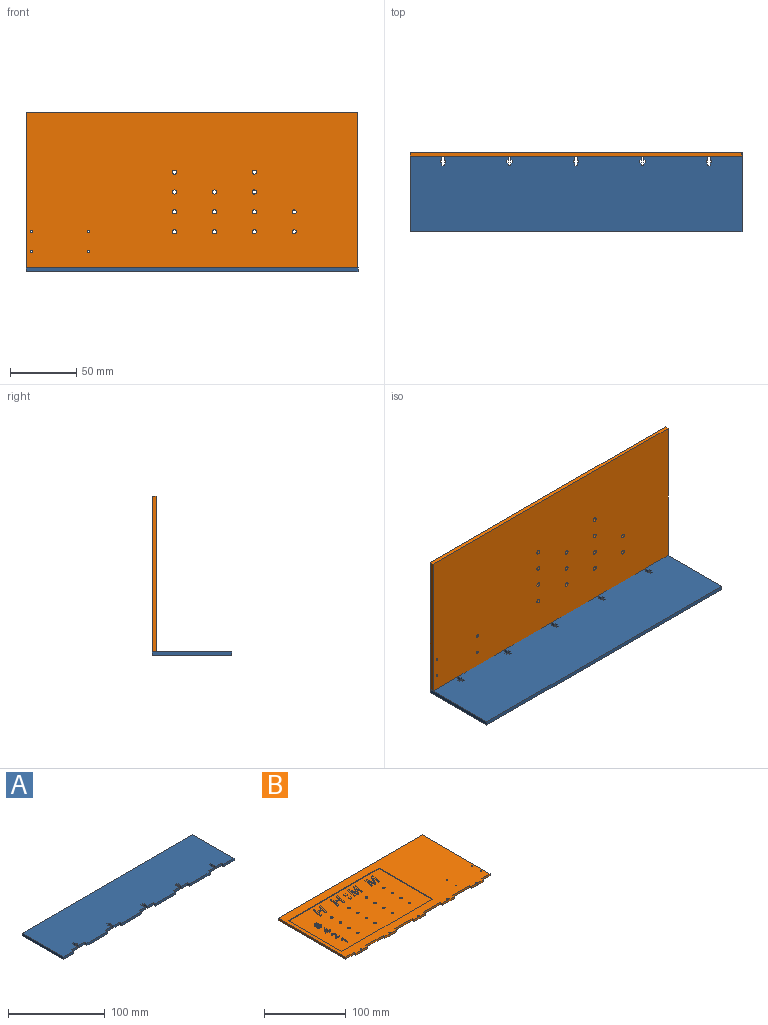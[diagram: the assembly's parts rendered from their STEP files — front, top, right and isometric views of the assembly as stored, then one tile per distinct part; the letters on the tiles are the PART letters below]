
ASSEMBLY  parts=2 mates=1
PART A: 86 faces, bbox 250x60x3 mm
  f0: plane 3x3mm, normal (-1,0,0), area 9mm2, adj f1,f83,f84,f85
  f1: plane 30x3mm, normal (0,-1,0), area 90mm2, adj f0,f2,f84,f85
  f2: plane 3x3mm, normal (1,0,0), area 9mm2, adj f1,f3,f84,f85
  f3: plane 9x3mm, normal (0,-1,0), area 27mm2, adj f2,f4,f84,f85
  f4: plane 3.04x3mm, normal (1,0,0), area 9.1mm2, adj f3,f5,f84,f85
  f5: plane 3x1mm, normal (0,1,0), area 3mm2, adj f4,f6,f84,f85
  f6: plane 3x2mm, normal (1,0,0), area 6mm2, adj f5,f7,f84,f85
  f7: plane 3x1mm, normal (0,-1,0), area 3mm2, adj f6,f8,f84,f85
  f8: plane 3x1.96mm, normal (1,0,0), area 5.9mm2, adj f7,f9,f84,f85
  f9: plane 3x2mm, normal (0,-1,0), area 6mm2, adj f8,f10,f84,f85
  f10: plane 3x1.96mm, normal (-1,0,0), area 5.9mm2, adj f9,f11,f84,f85
  f11: plane 3x1mm, normal (0,-1,0), area 3mm2, adj f10,f12,f84,f85
  f12: plane 3x2mm, normal (-1,0,0), area 6mm2, adj f11,f13,f84,f85
  f13: plane 3x1mm, normal (0,1,0), area 3mm2, adj f12,f14,f84,f85
  f14: plane 3.04x3mm, normal (-1,0,0), area 9.1mm2, adj f13,f15,f84,f85
  f15: plane 9x3mm, normal (0,-1,0), area 27mm2, adj f14,f16,f84,f85
  f16: plane 3x3mm, normal (-1,0,0), area 9mm2, adj f15,f17,f84,f85
  f17: plane 15x3mm, normal (0,-1,0), area 45mm2, adj f16,f18,f84,f85
  f18: plane 60x3mm, normal (1,0,0), area 180mm2, adj f17,f19,f84,f85
  f19: plane 250x3mm, normal (0,1,0), area 750mm2, adj f18,f20,f84,f85
  f20: plane 60x3mm, normal (-1,0,0), area 180mm2, adj f19,f21,f84,f85
  f21: plane 15x3mm, normal (0,-1,0), area 45mm2, adj f20,f22,f84,f85
  f22: plane 3x3mm, normal (1,0,0), area 9mm2, adj f21,f23,f84,f85
  f23: plane 9x3mm, normal (0,-1,0), area 27mm2, adj f22,f24,f84,f85
  f24: plane 3.04x3mm, normal (1,0,0), area 9.1mm2, adj f23,f25,f84,f85
  f25: plane 3x1mm, normal (0,1,0), area 3mm2, adj f24,f26,f84,f85
  f26: plane 3x2mm, normal (1,0,0), area 6mm2, adj f25,f27,f84,f85
  f27: plane 3x1mm, normal (0,-1,0), area 3mm2, adj f26,f28,f84,f85
  f28: plane 3x1.96mm, normal (1,0,0), area 5.9mm2, adj f27,f29,f84,f85
  f29: plane 3x2mm, normal (0,-1,0), area 6mm2, adj f28,f30,f84,f85
  f30: plane 3x1.96mm, normal (-1,0,0), area 5.9mm2, adj f29,f31,f84,f85
  f31: plane 3x1mm, normal (0,-1,0), area 3mm2, adj f30,f32,f84,f85
  f32: plane 3x2mm, normal (-1,0,0), area 6mm2, adj f31,f33,f84,f85
  f33: plane 3x1mm, normal (0,1,0), area 3mm2, adj f32,f34,f84,f85
  f34: plane 3.04x3mm, normal (-1,0,0), area 9.1mm2, adj f33,f35,f84,f85
  f35: plane 9x3mm, normal (0,-1,0), area 27mm2, adj f34,f36,f84,f85
  f36: plane 3x3mm, normal (-1,0,0), area 9mm2, adj f35,f37,f84,f85
  f37: plane 30x3mm, normal (0,-1,0), area 90mm2, adj f36,f38,f84,f85
  f38: plane 3x3mm, normal (1,0,0), area 9mm2, adj f37,f39,f84,f85
  f39: plane 9x3mm, normal (0,-1,0), area 27mm2, adj f38,f40,f84,f85
  f40: plane 3.04x3mm, normal (1,0,0), area 9.1mm2, adj f39,f41,f84,f85
  f41: plane 3x1mm, normal (0,1,0), area 3mm2, adj f40,f42,f84,f85
  f42: plane 3x2mm, normal (1,0,0), area 6mm2, adj f41,f43,f84,f85
  f43: plane 3x1mm, normal (0,-1,0), area 3mm2, adj f42,f44,f84,f85
  f44: plane 3x1.96mm, normal (1,0,0), area 5.9mm2, adj f43,f45,f84,f85
  f45: plane 3x2mm, normal (0,-1,0), area 6mm2, adj f44,f46,f84,f85
  f46: plane 3x1.96mm, normal (-1,0,0), area 5.9mm2, adj f45,f47,f84,f85
  f47: plane 3x1mm, normal (0,-1,0), area 3mm2, adj f46,f48,f84,f85
  f48: plane 3x2mm, normal (-1,0,0), area 6mm2, adj f47,f49,f84,f85
  f49: plane 3x1mm, normal (0,1,0), area 3mm2, adj f48,f50,f84,f85
  f50: plane 3.04x3mm, normal (-1,0,0), area 9.1mm2, adj f49,f51,f84,f85
  f51: plane 9x3mm, normal (0,-1,0), area 27mm2, adj f50,f52,f84,f85
  f52: plane 3x3mm, normal (-1,0,0), area 9mm2, adj f51,f53,f84,f85
  f53: plane 30x3mm, normal (0,-1,0), area 90mm2, adj f52,f54,f84,f85
  f54: plane 3x3mm, normal (1,0,0), area 9mm2, adj f53,f55,f84,f85
  f55: plane 9x3mm, normal (0,-1,0), area 27mm2, adj f54,f56,f84,f85
  f56: plane 3.04x3mm, normal (1,0,0), area 9.1mm2, adj f55,f57,f84,f85
  f57: plane 3x1mm, normal (0,1,0), area 3mm2, adj f56,f58,f84,f85
  f58: plane 3x2mm, normal (1,0,0), area 6mm2, adj f57,f59,f84,f85
  f59: plane 3x1mm, normal (0,-1,0), area 3mm2, adj f58,f60,f84,f85
  f60: plane 3x1.96mm, normal (1,0,0), area 5.9mm2, adj f59,f61,f84,f85
  f61: plane 3x2mm, normal (0,-1,0), area 6mm2, adj f60,f62,f84,f85
  f62: plane 3x1.96mm, normal (-1,0,0), area 5.9mm2, adj f61,f63,f84,f85
  f63: plane 3x1mm, normal (0,-1,0), area 3mm2, adj f62,f64,f84,f85
  f64: plane 3x2mm, normal (-1,0,0), area 6mm2, adj f63,f65,f84,f85
  f65: plane 3x1mm, normal (0,1,0), area 3mm2, adj f64,f66,f84,f85
  f66: plane 3.04x3mm, normal (-1,0,0), area 9.1mm2, adj f65,f67,f84,f85
  f67: plane 9x3mm, normal (0,-1,0), area 27mm2, adj f66,f68,f84,f85
  f68: plane 3x3mm, normal (-1,0,0), area 9mm2, adj f67,f69,f84,f85
  f69: plane 30x3mm, normal (0,-1,0), area 90mm2, adj f68,f70,f84,f85
  f70: plane 3x3mm, normal (1,0,0), area 9mm2, adj f69,f71,f84,f85
  f71: plane 9x3mm, normal (0,-1,0), area 27mm2, adj f70,f72,f84,f85
  f72: plane 3.04x3mm, normal (1,0,0), area 9.1mm2, adj f71,f73,f84,f85
  f73: plane 3x1mm, normal (0,1,0), area 3mm2, adj f72,f74,f84,f85
  f74: plane 3x2mm, normal (1,0,0), area 6mm2, adj f73,f75,f84,f85
  f75: plane 3x1mm, normal (0,-1,0), area 3mm2, adj f74,f76,f84,f85
  f76: plane 3x1.96mm, normal (1,0,0), area 5.9mm2, adj f75,f77,f84,f85
  f77: plane 3x2mm, normal (0,-1,0), area 6mm2, adj f76,f78,f84,f85
  f78: plane 3x1.96mm, normal (-1,0,0), area 5.9mm2, adj f77,f79,f84,f85
  f79: plane 3x1mm, normal (0,-1,0), area 3mm2, adj f78,f80,f84,f85
  f80: plane 3x2mm, normal (-1,0,0), area 6mm2, adj f79,f81,f84,f85
  f81: plane 3x1mm, normal (0,1,0), area 3mm2, adj f80,f82,f84,f85
  f82: plane 3.04x3mm, normal (-1,0,0), area 9.1mm2, adj f81,f83,f84,f85
  f83: plane 9x3mm, normal (0,-1,0), area 27mm2, adj f0,f82,f84,f85
  f84: plane 250x60mm, normal (0,0,1), area 14610mm2, adj f0,f1,f2,f3,f4,f5,f6,f7
  f85: plane 250x60mm, normal (0,0,-1), area 14610mm2, adj f0,f1,f2,f3,f4,f5,f6,f7
PART B: 219 faces, bbox 250x120x3 mm
  f0: cylinder r=1.55mm len=3.1mm, axis (0,0,1), area 19.5mm2, adj f46,f180
  f1: cylinder r=1.55mm len=3.1mm, axis (0,0,1), area 19.5mm2, adj f46,f180
  f2: cylinder r=1.55mm len=3.1mm, axis (0,0,1), area 19.5mm2, adj f46,f180
  f3: cylinder r=1.55mm len=3.1mm, axis (0,0,1), area 19.5mm2, adj f46,f180
  f4: cylinder r=1.55mm len=3.1mm, axis (0,0,1), area 19.5mm2, adj f46,f180
  f5: cylinder r=1.55mm len=3.1mm, axis (0,0,1), area 19.5mm2, adj f46,f180
  f6: cylinder r=1.55mm len=3.1mm, axis (0,0,1), area 19.5mm2, adj f46,f180
  f7: cylinder r=1.55mm len=3.1mm, axis (0,0,1), area 19.5mm2, adj f46,f180
  f8: cylinder r=1.55mm len=3.1mm, axis (0,0,1), area 19.5mm2, adj f46,f180
  f9: cylinder r=1.55mm len=3.1mm, axis (0,0,1), area 19.5mm2, adj f46,f180
  f10: cylinder r=1.55mm len=3.1mm, axis (0,0,1), area 19.5mm2, adj f46,f180
  f11: cylinder r=1.55mm len=3.1mm, axis (0,0,1), area 19.5mm2, adj f46,f180
  f12: cylinder r=1.55mm len=3.1mm, axis (0,0,1), area 19.5mm2, adj f46,f180
  f13: plane 30x3mm, normal (0,-1,0), area 90mm2, adj f14,f41,f46,f47
  f14: plane 3x3mm, normal (-1,0,0), area 9mm2, adj f13,f15,f46,f47
  f15: plane 20x3mm, normal (0,-1,0), area 60mm2, adj f14,f16,f46,f47
  f16: plane 3x3mm, normal (1,0,0), area 9mm2, adj f15,f17,f46,f47
  f17: plane 30x3mm, normal (0,-1,0), area 90mm2, adj f16,f18,f46,f47
  f18: plane 3x3mm, normal (-1,0,0), area 9mm2, adj f17,f19,f46,f47
  f19: plane 20x3mm, normal (0,-1,0), area 60mm2, adj f18,f20,f46,f47
  f20: plane 3x3mm, normal (1,0,0), area 9mm2, adj f19,f21,f46,f47
  f21: plane 30x3mm, normal (0,-1,0), area 90mm2, adj f20,f22,f46,f47
  f22: plane 3x3mm, normal (-1,0,0), area 9mm2, adj f21,f23,f46,f47
  f23: plane 20x3mm, normal (0,-1,0), area 60mm2, adj f22,f24,f46,f47
  f24: plane 3x3mm, normal (1,0,0), area 9mm2, adj f23,f25,f46,f47
  f25: plane 30x3mm, normal (0,-1,0), area 90mm2, adj f24,f26,f46,f47
  f26: plane 3x3mm, normal (-1,0,0), area 9mm2, adj f25,f27,f46,f47
  f27: plane 20x3mm, normal (0,-1,0), area 60mm2, adj f26,f28,f46,f47
  f28: plane 3x3mm, normal (1,0,0), area 9mm2, adj f27,f29,f46,f47
  f29: plane 15x3mm, normal (0,-1,0), area 45mm2, adj f28,f30,f46,f47
  f30: plane 117x3mm, normal (1,0,0), area 351mm2, adj f29,f31,f46,f47
  f31: plane 250x3mm, normal (0,1,0), area 750mm2, adj f30,f32,f46,f47
  f32: plane 117x3mm, normal (-1,0,0), area 351mm2, adj f31,f33,f46,f47
  f33: plane 15x3mm, normal (0,-1,0), area 45mm2, adj f32,f34,f46,f47
  f34: plane 3x3mm, normal (-1,0,0), area 9mm2, adj f33,f35,f46,f47
  f35: plane 20x3mm, normal (0,-1,0), area 60mm2, adj f34,f41,f46,f47
  f36: cylinder r=1.05mm len=3mm, axis (0,0,1), area 19.8mm2, adj f46,f47
  f37: cylinder r=1.05mm len=3mm, axis (0,0,1), area 19.8mm2, adj f46,f47
  f38: cylinder r=1.05mm len=3mm, axis (0,0,1), area 19.8mm2, adj f46,f47
  f39: cylinder r=1.05mm len=3mm, axis (0,0,1), area 19.8mm2, adj f46,f47
  f40: cylinder r=1.05mm len=3mm, axis (0,0,1), area 19.8mm2, adj f46,f47
  f41: plane 3x3mm, normal (1,0,0), area 9mm2, adj f13,f35,f46,f47
  f42: cylinder r=0.89mm len=3mm, axis (0,0,1), area 16.8mm2, adj f46,f47
  f43: cylinder r=0.89mm len=3mm, axis (0,0,1), area 16.8mm2, adj f46,f47
  f44: cylinder r=0.89mm len=3mm, axis (0,0,1), area 16.8mm2, adj f46,f47
  f45: cylinder r=0.89mm len=3mm, axis (0,0,1), area 16.8mm2, adj f46,f47
  f46: plane 250x120mm, normal (0,0,-1), area 29424.6mm2, adj f0,f1,f2,f3,f4,f5,f6,f7
  f47: plane 250x120mm, normal (0,0,1), area 14951.8mm2, adj f13,f14,f15,f16,f17,f18,f19,f20
  f48: plane 92.55x1mm, normal (1,0,0), area 92.5mm2, adj f47,f49,f179,f180
  f49: plane 157.45x1mm, normal (0,1,0), area 157.4mm2, adj f47,f48,f50,f180
  f50: plane 92.55x1mm, normal (-1,0,0), area 92.5mm2, adj f47,f49,f179,f180
  f51: plane 6.67x1mm, normal (1,0,0), area 6.7mm2, adj f52,f166,f180,f193
  f52: plane 1.47x1mm, normal (0,1,0), area 1.5mm2, adj f51,f53,f180,f193
  f53: plane 1.02x1mm, normal (1,0,0), area 1mm2, adj f52,f54,f180,f193
  f54: plane 1.47x1mm, normal (0,-1,0), area 1.5mm2, adj f53,f55,f180,f193
  f55: plane 2.28x1mm, normal (1,0,0), area 2.3mm2, adj f54,f56,f180,f193
  f56: plane 1.08x1mm, normal (0,-1,0), area 1.1mm2, adj f55,f57,f180,f193
  f57: plane 2.28x1mm, normal (-1,0,0), area 2.3mm2, adj f56,f58,f180,f193
  f58: plane 4.82x1mm, normal (0,-1,0), area 4.8mm2, adj f57,f59,f180,f193
  f59: plane 1x0.98mm, normal (-1,0,0), area 1mm2, adj f58,f60,f180,f193
  f60: plane 6.71x4.71mm, normal (-0.82,0.57,0), area 8.2mm2, adj f59,f166,f180,f193
  f61: plane 7.8x1mm, normal (0,-1,0), area 7.8mm2, adj f62,f167,f180,f192
  f62: plane 6.64x1.29mm, normal (0.98,-0.19,0), area 6.8mm2, adj f61,f63,f180,f192
  f63: plane 1.94x1mm, normal (0,-1,0), area 1.9mm2, adj f62,f64,f180,f192
  f64: plane 14.33x2.79mm, normal (-0.98,0.19,0), area 14.6mm2, adj f63,f65,f180,f192
  f65: plane 1.94x1mm, normal (0,1,0), area 1.9mm2, adj f64,f66,f180,f192
  f66: plane 6.06x1.18mm, normal (0.98,-0.19,0), area 6.2mm2, adj f65,f67,f180,f192
  f67: plane 7.8x1mm, normal (0,1,0), area 7.8mm2, adj f66,f68,f180,f192
  f68: plane 6.06x1.18mm, normal (-0.98,0.19,0), area 6.2mm2, adj f67,f69,f180,f192
  f69: plane 1.89x1mm, normal (0,1,0), area 1.9mm2, adj f68,f70,f180,f192
  f70: plane 14.33x2.79mm, normal (0.98,-0.19,0), area 14.6mm2, adj f69,f71,f180,f192
  f71: plane 1.89x1mm, normal (0,-1,0), area 1.9mm2, adj f70,f167,f180,f192
  f72: plane 1.89x1mm, normal (0,1,0), area 1.9mm2, adj f73,f168,f180,f191
  f73: plane 14.33x2.79mm, normal (0.98,-0.19,0), area 14.6mm2, adj f72,f74,f180,f191
  f74: plane 1.89x1mm, normal (0,-1,0), area 1.9mm2, adj f73,f75,f180,f191
  f75: plane 6.64x1.29mm, normal (-0.98,0.19,0), area 6.8mm2, adj f74,f76,f180,f191
  f76: plane 7.8x1mm, normal (0,-1,0), area 7.8mm2, adj f75,f77,f180,f191
  f77: plane 6.64x1.29mm, normal (0.98,-0.19,0), area 6.8mm2, adj f76,f78,f180,f191
  f78: plane 1.94x1mm, normal (0,-1,0), area 1.9mm2, adj f77,f79,f180,f191
  f79: plane 14.33x2.79mm, normal (-0.98,0.19,0), area 14.6mm2, adj f78,f80,f180,f191
  f80: plane 1.94x1mm, normal (0,1,0), area 1.9mm2, adj f79,f81,f180,f191
  f81: plane 6.06x1.18mm, normal (0.98,-0.19,0), area 6.2mm2, adj f80,f82,f180,f191
  f82: plane 7.8x1mm, normal (0,1,0), area 7.8mm2, adj f81,f168,f180,f191
  f83: plane 3.06x1mm, normal (1,0,0), area 3.1mm2, adj f84,f169,f180,f190
  f84: plane 3.13x1mm, normal (0,-1,0), area 3.1mm2, adj f83,f85,f180,f190
  f85: plane 3.06x1mm, normal (-1,0,0), area 3.1mm2, adj f84,f169,f180,f190
  f86: plane 3.05x1mm, normal (1,0,0), area 3.1mm2, adj f87,f170,f180,f189
  f87: plane 3.13x1mm, normal (0,-1,0), area 3.1mm2, adj f86,f88,f180,f189
  f88: plane 3.05x1mm, normal (-1,0,0), area 3.1mm2, adj f87,f170,f180,f189
  f89: plane 9.86x5.63mm, normal (-0.87,0.5,0), area 11.3mm2, adj f90,f171,f180,f188
  f90: plane 2.6x1mm, normal (0,1,0), area 2.6mm2, adj f89,f91,f180,f188
  f91: plane 14.33x2.78mm, normal (0.98,-0.19,0), area 14.6mm2, adj f90,f92,f180,f188
  f92: plane 1.75x1mm, normal (0,-1,0), area 1.7mm2, adj f91,f93,f180,f188
  f93: plane 9.44x1.83mm, normal (-0.98,0.19,0), area 9.6mm2, adj f92,f94,f180,f188
  f94: extruded ~3.05x1mm, area 3.1mm2, adj f93,f95,f180,f188
  f95: extruded ~2.85x1.47mm, area 3.2mm2, adj f94,f96,f180,f188
  f96: plane 9.65x5.57mm, normal (0.87,-0.5,0), area 11.1mm2, adj f95,f97,f180,f188
  f97: plane 1.26x1mm, normal (0,-1,0), area 1.3mm2, adj f96,f98,f180,f188
  f98: plane 9.65x1.88mm, normal (-0.98,-0.19,0), area 9.8mm2, adj f97,f99,f180,f188
  f99: extruded ~2.85x1mm, area 2.9mm2, adj f98,f100,f180,f188
  f100: extruded ~1.91x1mm, area 1.9mm2, adj f99,f101,f180,f188
  f101: extruded ~10.58x2.04mm, area 10.8mm2, adj f100,f102,f180,f188
  f102: plane 1.73x1mm, normal (0,-1,0), area 1.7mm2, adj f101,f103,f180,f188
  f103: plane 14.33x2.78mm, normal (-0.98,0.19,0), area 14.6mm2, adj f102,f104,f180,f188
  f104: plane 2.4x1mm, normal (0,1,0), area 2.4mm2, adj f103,f105,f180,f188
  f105: plane 9.94x1.92mm, normal (0.98,0.19,0), area 10.1mm2, adj f104,f106,f180,f188
  f106: extruded ~2.09x1mm, area 2.1mm2, adj f105,f171,f180,f188
  f107: extruded ~1.72x1.21mm, area 2.1mm2, adj f108,f172,f180,f187
  f108: extruded ~1.47x1mm, area 1.6mm2, adj f107,f109,f180,f187
  f109: extruded ~1.97x1mm, area 2.2mm2, adj f108,f110,f180,f187
  f110: extruded ~2.36x1mm, area 2.5mm2, adj f109,f111,f180,f187
  f111: extruded ~2.44x1mm, area 2.6mm2, adj f110,f112,f180,f187
  f112: extruded ~1.97x1mm, area 2.2mm2, adj f111,f113,f180,f187
  f113: extruded ~2.65x2.07mm, area 3.6mm2, adj f112,f114,f180,f187
  f114: extruded ~1.34x1.14mm, area 1.8mm2, adj f113,f115,f180,f187
  f115: extruded ~1.37x1mm, area 1.5mm2, adj f114,f116,f180,f187
  f116: extruded ~1.72x1mm, area 2mm2, adj f115,f117,f180,f187
  f117: extruded ~2.13x1mm, area 2.3mm2, adj f116,f118,f180,f187
  f118: extruded ~2.15x1mm, area 2.3mm2, adj f117,f119,f180,f187
  f119: extruded ~1.74x1mm, area 2mm2, adj f118,f120,f180,f187
  f120: extruded ~1.34x1mm, area 1.4mm2, adj f119,f172,f180,f187
  f121: plane 7.07x1mm, normal (-1,0,0), area 7.1mm2, adj f122,f174,f180,f185
  f122: extruded ~1.67x1mm, area 1.7mm2, adj f121,f123,f180,f185
  f123: extruded ~1x0.32mm, area 0.4mm2, adj f122,f124,f180,f185
  f124: extruded ~1.61x1.32mm, area 2.1mm2, adj f123,f125,f180,f185
  f125: plane 1x0.77mm, normal (-0.79,-0.61,0), area 1mm2, adj f124,f126,f180,f185
  f126: plane 2.62x2.03mm, normal (-0.61,0.79,0), area 3.3mm2, adj f125,f127,f180,f185
  f127: plane 1x0.95mm, normal (0,1,0), area 0.9mm2, adj f126,f128,f180,f185
  f128: plane 9.92x1mm, normal (1,0,0), area 9.9mm2, adj f127,f174,f180,f185
  f129: extruded ~1.72x1.57mm, area 2.3mm2, adj f130,f176,f180,f183
  f130: extruded ~1x1mm, area 1.2mm2, adj f129,f131,f180,f183
  f131: extruded ~1.05x1mm, area 1.1mm2, adj f130,f132,f180,f183
  f132: extruded ~1.26x1mm, area 1.4mm2, adj f131,f133,f180,f183
  f133: extruded ~1.34x1mm, area 1.5mm2, adj f132,f134,f180,f183
  f134: extruded ~1.17x1mm, area 1.2mm2, adj f133,f135,f180,f183
  f135: extruded ~1.23x1mm, area 1.4mm2, adj f134,f136,f180,f183
  f136: plane 1x0.77mm, normal (-0.79,-0.61,0), area 1mm2, adj f135,f137,f180,f183
  f137: extruded ~2.98x1.14mm, area 3.3mm2, adj f136,f138,f180,f183
  f138: extruded ~2.19x1mm, area 2.4mm2, adj f137,f139,f180,f183
  f139: extruded ~1.92x1mm, area 2.1mm2, adj f138,f140,f180,f183
  f140: extruded ~1.87x1mm, area 2mm2, adj f139,f141,f180,f183
  f141: extruded ~2.33x1.98mm, area 3.1mm2, adj f140,f142,f180,f183
  f142: plane 2.17x2.12mm, normal (0.7,-0.71,0), area 3mm2, adj f141,f143,f180,f183
  f143: plane 1x0.05mm, normal (1,0,0), area 0.1mm2, adj f142,f144,f180,f183
  f144: plane 5.1x1mm, normal (0,1,0), area 5.1mm2, adj f143,f145,f180,f183
  f145: plane 1.04x1mm, normal (1,0,0), area 1mm2, adj f144,f146,f180,f183
  f146: plane 6.52x1mm, normal (0,-1,0), area 6.5mm2, adj f145,f147,f180,f183
  f147: plane 1x0.97mm, normal (-1,0,0), area 1mm2, adj f146,f176,f180,f183
  f148: plane 2.17x1.06mm, normal (-0.9,0.44,0), area 2.4mm2, adj f149,f178,f180,f181
  f149: plane 9.86x5.63mm, normal (-0.87,0.5,0), area 11.3mm2, adj f148,f150,f180,f181
  f150: plane 2.6x1mm, normal (0,1,0), area 2.6mm2, adj f149,f151,f180,f181
  f151: plane 14.33x2.78mm, normal (0.98,-0.19,0), area 14.6mm2, adj f150,f152,f180,f181
  f152: plane 1.75x1mm, normal (0,-1,0), area 1.7mm2, adj f151,f153,f180,f181
  f153: plane 9.44x1.83mm, normal (-0.98,0.19,0), area 9.6mm2, adj f152,f154,f180,f181
  f154: extruded ~3.05x1mm, area 3.1mm2, adj f153,f155,f180,f181
  f155: extruded ~2.85x1.47mm, area 3.2mm2, adj f154,f156,f180,f181
  f156: plane 9.65x5.57mm, normal (0.87,-0.5,0), area 11.1mm2, adj f155,f157,f180,f181
  f157: plane 1.26x1mm, normal (0,-1,0), area 1.3mm2, adj f156,f158,f180,f181
  f158: plane 9.65x1.88mm, normal (-0.98,-0.19,0), area 9.8mm2, adj f157,f159,f180,f181
  f159: extruded ~2.85x1mm, area 2.9mm2, adj f158,f160,f180,f181
  f160: extruded ~1.91x1mm, area 1.9mm2, adj f159,f161,f180,f181
  f161: extruded ~10.58x2.04mm, area 10.8mm2, adj f160,f162,f180,f181
  f162: plane 1.73x1mm, normal (0,-1,0), area 1.7mm2, adj f161,f163,f180,f181
  f163: plane 14.33x2.78mm, normal (-0.98,0.19,0), area 14.6mm2, adj f162,f164,f180,f181
  f164: plane 2.4x1mm, normal (0,1,0), area 2.4mm2, adj f163,f165,f180,f181
  f165: plane 9.94x1.92mm, normal (0.98,0.19,0), area 10.1mm2, adj f164,f178,f180,f181
  f166: plane 1.19x1mm, normal (0,1,0), area 1.2mm2, adj f51,f60,f180,f193
  f167: plane 6.64x1.29mm, normal (-0.98,0.19,0), area 6.8mm2, adj f61,f71,f180,f192
  f168: plane 6.06x1.18mm, normal (-0.98,0.19,0), area 6.2mm2, adj f72,f82,f180,f191
  f169: plane 3.13x1mm, normal (0,1,0), area 3.1mm2, adj f83,f85,f180,f190
  f170: plane 3.13x1mm, normal (0,1,0), area 3.1mm2, adj f86,f88,f180,f189
  f171: plane 2.17x1.06mm, normal (-0.9,0.44,0), area 2.4mm2, adj f89,f106,f180,f188
  f172: extruded ~1.45x1.1mm, area 1.8mm2, adj f107,f120,f180,f187
  f173: cylinder r=1.55mm len=3.1mm, axis (0,0,1), area 9.7mm2, adj f180,f186
  f174: plane 1.1x1mm, normal (0,-1,0), area 1.1mm2, adj f121,f128,f180,f185
  f175: cylinder r=1.55mm len=3.1mm, axis (0,0,1), area 9.7mm2, adj f180,f184
  f176: plane 2.62x2.61mm, normal (-0.71,0.71,0), area 3.7mm2, adj f129,f147,f180,f183
  f177: cylinder r=1.55mm len=3.1mm, axis (0,0,1), area 9.7mm2, adj f180,f182
  f178: extruded ~2.09x1mm, area 2.1mm2, adj f148,f165,f180,f181
  f179: plane 157.45x1mm, normal (0,-1,0), area 157.4mm2, adj f47,f48,f50,f180
  f180: plane 157.45x92.55mm, normal (0,0,1), area 13990.9mm2, adj f0,f1,f2,f3,f4,f5,f6,f7
  f181: plane 16.71x14.33mm, normal (0,0,1), area 92.3mm2, adj f148,f149,f150,f151,f152,f153,f154,f155
  f182: plane 3.1x3.1mm, normal (0,0,1), area 7.5mm2, adj f177
  f183: plane 10.06x6.52mm, normal (0,0,1), area 21.7mm2, adj f129,f130,f131,f132,f133,f134,f135,f136
  f184: plane 3.1x3.1mm, normal (0,0,1), area 7.5mm2, adj f175
  f185: plane 9.92x3.57mm, normal (0,0,1), area 13.5mm2, adj f121,f122,f123,f124,f125,f126,f127,f128
  f186: plane 3.1x3.1mm, normal (0,0,1), area 7.5mm2, adj f173
  f187: plane 10.19x6.52mm, normal (0,0,1), area 29.1mm2, adj f107,f108,f109,f110,f111,f112,f113,f114
  f188: plane 16.71x14.33mm, normal (0,0,1), area 92.3mm2, adj f89,f90,f91,f92,f93,f94,f95,f96
  f189: plane 3.13x3.05mm, normal (0,0,1), area 9.5mm2, adj f86,f87,f88,f170
  f190: plane 3.13x3.06mm, normal (0,0,1), area 9.6mm2, adj f83,f84,f85,f169
  f191: plane 14.42x14.33mm, normal (0,0,1), area 67.7mm2, adj f72,f73,f74,f75,f76,f77,f78,f79
  f192: plane 14.42x14.33mm, normal (0,0,1), area 67.7mm2, adj f61,f62,f63,f64,f65,f66,f67,f68
  f193: plane 9.97x7.37mm, normal (0,0,1), area 23.7mm2, adj f51,f52,f53,f54,f55,f56,f57,f58
  f194: extruded ~1.47x1mm, area 1.8mm2, adj f187,f195,f201,f202
  f195: extruded ~1.26x1mm, area 1.4mm2, adj f187,f194,f196,f202
  f196: extruded ~1.27x1mm, area 1.4mm2, adj f187,f195,f197,f202
  f197: extruded ~1.59x1mm, area 1.7mm2, adj f187,f196,f198,f202
  f198: extruded ~1.57x1mm, area 1.7mm2, adj f187,f197,f199,f202
  f199: extruded ~1.3x1mm, area 1.5mm2, adj f187,f198,f200,f202
  f200: extruded ~1.17x1mm, area 1.3mm2, adj f187,f199,f201,f202
  f201: extruded ~1.84x1mm, area 2.1mm2, adj f187,f194,f200,f202
  f202: plane 4.29x3.94mm, normal (0,0,1), area 12.9mm2, adj f194,f195,f196,f197,f198,f199,f200,f201
  f203: extruded ~1.09x1mm, area 1.2mm2, adj f187,f204,f210,f211
  f204: extruded ~1.35x1mm, area 1.4mm2, adj f187,f203,f205,f211
  f205: extruded ~1.33x1mm, area 1.4mm2, adj f187,f204,f206,f211
  f206: extruded ~1.09x1mm, area 1.2mm2, adj f187,f205,f207,f211
  f207: extruded ~1.07x1mm, area 1.2mm2, adj f187,f206,f208,f211
  f208: extruded ~1.48x1mm, area 1.7mm2, adj f187,f207,f209,f211
  f209: extruded ~1.37x1mm, area 1.6mm2, adj f187,f208,f210,f211
  f210: extruded ~1.09x1mm, area 1.2mm2, adj f187,f203,f209,f211
  f211: plane 3.66x3.46mm, normal (0,0,1), area 9.6mm2, adj f203,f204,f205,f206,f207,f208,f209,f210
  f212: plane 3.3x1mm, normal (-1,0,0), area 3.3mm2, adj f193,f213,f217,f218
  f213: extruded ~2.19x1mm, area 2.2mm2, adj f193,f212,f214,f218
  f214: plane 1x0.05mm, normal (0,-1,0), area 0.1mm2, adj f193,f213,f215,f218
  f215: extruded ~1.08x1mm, area 1.2mm2, adj f193,f214,f216,f218
  f216: plane 4.41x3.1mm, normal (0.82,-0.58,0), area 5.4mm2, adj f193,f215,f217,f218
  f217: plane 3.7x1mm, normal (0,1,0), area 3.7mm2, adj f193,f212,f216,f218
  f218: plane 5.49x3.77mm, normal (0,0,1), area 9.8mm2, adj f212,f213,f214,f215,f216,f217
PLACE A rot(axis=(1,0,0),180deg) t=(0,66.65,3)mm
PLACE B rot(axis=(0,0.71,0.71),180deg) t=(42.69,34.82,106.73)mm
MATE fastened B.f37 <-> A.f69  axis (0,1,0) through (21.37,34.82,1.5)mm
